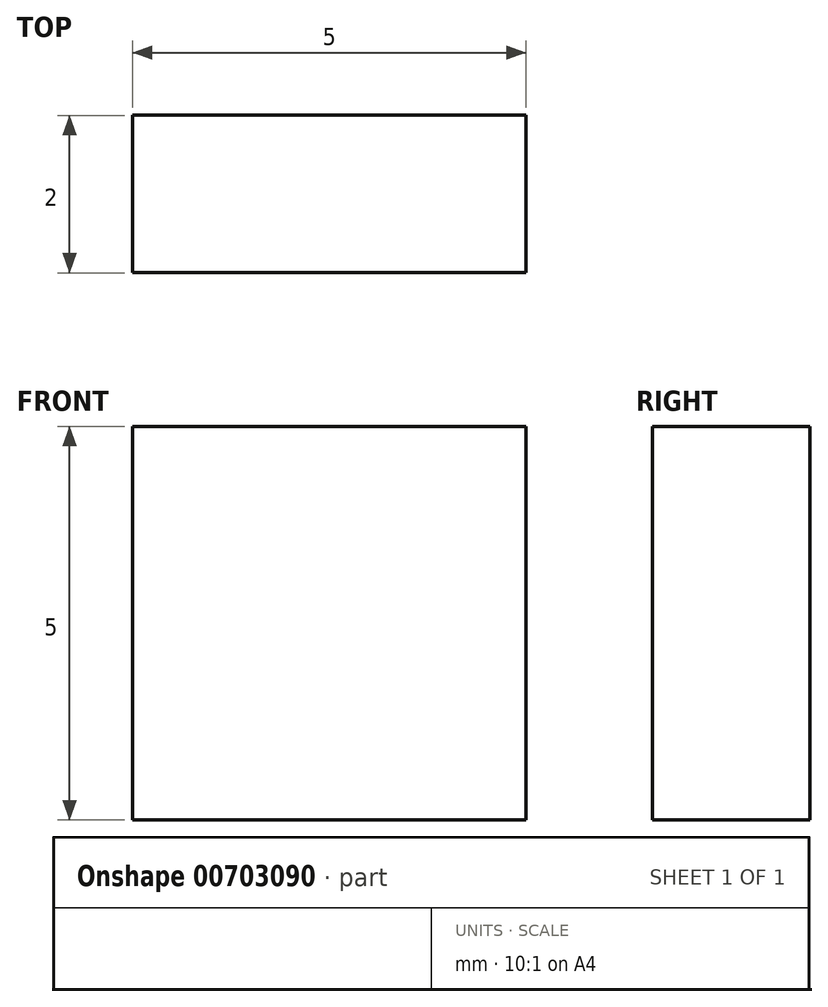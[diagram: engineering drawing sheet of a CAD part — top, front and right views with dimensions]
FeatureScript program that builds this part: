
annotation { "Feature Type Name" : "Feature", "Feature Type Description" : "" }
export const myFeature = defineFeature(function(context is Context, id is Id, definition is map)
    precondition{}
    {
        {
            var Q0;
            Q0=qCreatedBy(makeId("Top.planeOp"),FACE);
            var sketch = newSketch(context, id + "F0", { "sketchPlane" : qUnion([Q0])});
            skLineSegment(sketch, "E0.bottom", {"start": v(-7.56, 1.27) * mm, "end": v(-2.56, 1.27) * mm});
            skLineSegment(sketch, "E0.top", {"start": v(-7.56, -0.73) * mm, "end": v(-2.56, -0.73) * mm});
            skLineSegment(sketch, "E0.left", {"start": v(-7.56, 1.27) * mm, "end": v(-7.56, -0.73) * mm});
            skLineSegment(sketch, "E0.right", {"start": v(-2.56, 1.27) * mm, "end": v(-2.56, -0.73) * mm});
            skSolve(sketch);
        }
        {
            var Q0;
            Q0=makeQuery(id+"F0.imprint","IMPRINT",FACE,{"disambiguationData":[TD([[makeQuery(id+"F0.imprint","IMPRINT",EDGE,{"derivedFrom":sQuery(id+"F0.wireOp",EDGE,"E0.bottom")}),-1.0]])]});
            extrude(context, id + "F1", {"entities" : qUnion([Q0]), "depth" : 5 * mm, "offsetDistance" : 25 * mm});
        }
    });
